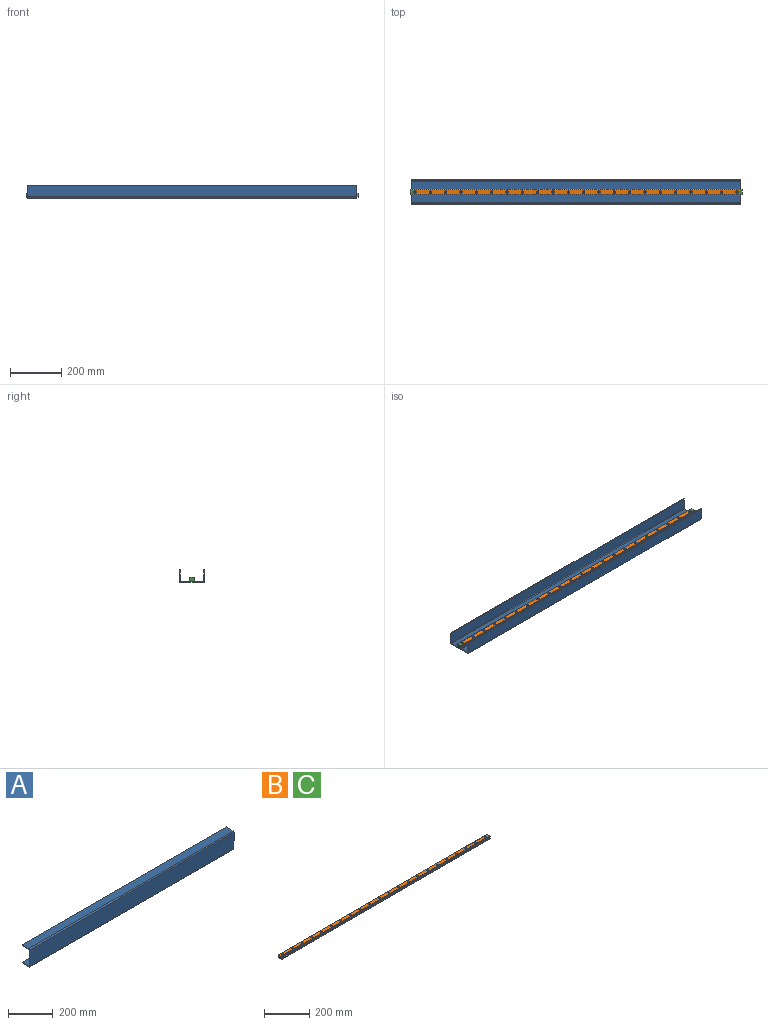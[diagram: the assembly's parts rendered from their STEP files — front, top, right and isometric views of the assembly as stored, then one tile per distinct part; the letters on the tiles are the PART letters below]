
ASSEMBLY  parts=3 mates=1
PART A: 14 faces, bbox 1290x50x100 mm
  f0: plane 1290x44mm, normal (0,0,1), area 56760mm2, adj f1,f11,f12,f13
  f1: cylinder r=6mm len=1290mm, axis (-1,0,0), area 12158mm2, adj f0,f2,f12,f13
  f2: plane 1290x88mm, normal (0,-1,0), area 113520mm2, adj f1,f3,f12,f13
  f3: cylinder r=6mm len=1290mm, axis (-1,0,0), area 12158mm2, adj f2,f4,f12,f13
  f4: plane 1290x44mm, normal (0,0,-1), area 56760mm2, adj f3,f5,f12,f13
  f5: plane 1290x4mm, normal (0,1,0), area 5160mm2, adj f4,f6,f12,f13
  f6: plane 1290x43mm, normal (0,0,1), area 55470mm2, adj f5,f7,f12,f13
  f7: cylinder r=3mm len=1290mm, axis (-1,0,0), area 6079mm2, adj f6,f8,f12,f13
  f8: plane 1290x86mm, normal (0,1,0), area 110940mm2, adj f7,f9,f12,f13
  f9: cylinder r=3mm len=1290mm, axis (-1,0,0), area 6079mm2, adj f8,f10,f12,f13
  f10: plane 1290x43mm, normal (0,0,-1), area 55470mm2, adj f9,f11,f12,f13
  f11: plane 1290x4mm, normal (0,1,0), area 5160mm2, adj f0,f10,f12,f13
  f12: plane 100x50mm, normal (1,0,0), area 756.4mm2, adj f0,f1,f2,f3,f4,f5,f6,f7
  f13: plane 100x50mm, normal (-1,0,0), area 756.4mm2, adj f0,f1,f2,f3,f4,f5,f6,f7
PART B: 100 faces, bbox 1300x20x16.5 mm
  f0: cylinder r=1.8mm len=1300mm, axis (-1,0,0), area 2943.1mm2, adj f1,f31,f32,f33
  f1: cylinder r=0.2mm len=1300mm, axis (-1,0,0), area 370.5mm2, adj f0,f2,f32,f33
  f2: plane 1300x16.31mm, normal (0,0,1), area 19645.8mm2, adj f1,f3,f32,f33,f34,f37,f40,f43
  f3: cylinder r=0.2mm len=1300mm, axis (-1,0,0), area 370.5mm2, adj f2,f4,f32,f33
  f4: cylinder r=1.8mm len=1300mm, axis (-1,0,0), area 2943mm2, adj f3,f5,f32,f33
  f5: cylinder r=0.2mm len=1300mm, axis (-1,0,0), area 364.4mm2, adj f4,f6,f32,f33
  f6: plane 1300x1.53mm, normal (0,-1,0), area 1984.4mm2, adj f5,f7,f32,f33
  f7: cylinder r=0.2mm len=1300mm, axis (-1,0,0), area 364.4mm2, adj f6,f8,f32,f33
  f8: cylinder r=1.8mm len=1300mm, axis (-1,0,0), area 3506.9mm2, adj f7,f9,f32,f33
  f9: cylinder r=0.2mm len=1300mm, axis (-1,0,0), area 228.9mm2, adj f8,f10,f32,f33
  f10: plane 1300x0.14mm, normal (0,-0.71,-0.71), area 254.9mm2, adj f9,f11,f32,f33
  f11: cylinder r=0.5mm len=1300mm, axis (-1,0,0), area 510.5mm2, adj f10,f12,f32,f33
  f12: plane 1300x4.09mm, normal (0,-1,0), area 5311.4mm2, adj f11,f13,f32,f33
  f13: cylinder r=0.5mm len=1300mm, axis (-1,0,0), area 510.5mm2, adj f12,f14,f32,f33
  f14: plane 1300x1.78mm, normal (0,-0.71,0.71), area 3273.1mm2, adj f13,f15,f32,f33
  f15: cylinder r=0.25mm len=1300mm, axis (-1,0,0), area 255.3mm2, adj f14,f16,f32,f33
  f16: plane 1300x2.9mm, normal (0,-1,0), area 3765.4mm2, adj f15,f17,f32,f33
  f17: plane 1300x1mm, normal (0,-0.71,-0.71), area 1838.4mm2, adj f16,f18,f32,f33
  f18: plane 1300x18mm, normal (0,0,-1), area 22778mm2, adj f17,f19,f32,f33,f36,f39,f42,f45
  f19: plane 1300x1mm, normal (0,0.71,-0.71), area 1838.5mm2, adj f18,f20,f32,f33
  f20: plane 1300x2.9mm, normal (0,1,0), area 3765.4mm2, adj f19,f21,f32,f33
  f21: cylinder r=0.25mm len=1300mm, axis (-1,0,0), area 255.3mm2, adj f20,f22,f32,f33
  f22: plane 1300x1.78mm, normal (0,0.71,0.71), area 3273.1mm2, adj f21,f23,f32,f33
  f23: cylinder r=0.5mm len=1300mm, axis (-1,0,0), area 510.5mm2, adj f22,f24,f32,f33
  f24: plane 1300x4.09mm, normal (0,1,0), area 5311.6mm2, adj f23,f25,f32,f33
  f25: cylinder r=0.5mm len=1300mm, axis (-1,0,0), area 510.5mm2, adj f24,f26,f32,f33
  f26: plane 1300x0.14mm, normal (0,0.71,-0.71), area 254.8mm2, adj f25,f27,f32,f33
  f27: cylinder r=0.2mm len=1300mm, axis (-1,0,0), area 228.9mm2, adj f26,f28,f32,f33
  f28: cylinder r=1.8mm len=1300mm, axis (-1,0,0), area 3506.9mm2, adj f27,f29,f32,f33
  f29: cylinder r=0.2mm len=1300mm, axis (-1,0,0), area 364.4mm2, adj f28,f30,f32,f33
  f30: plane 1300x1.53mm, normal (0,1,0), area 1984.4mm2, adj f29,f31,f32,f33
  f31: cylinder r=0.2mm len=1300mm, axis (-1,0,0), area 364.4mm2, adj f0,f30,f32,f33
  f32: plane 20x16.5mm, normal (1,0,0), area 295.9mm2, adj f0,f1,f2,f3,f4,f5,f6,f7
  f33: plane 20x16.5mm, normal (-1,0,0), area 295.9mm2, adj f0,f1,f2,f3,f4,f5,f6,f7
  f34: cylinder r=4.75mm len=9.5mm, axis (0,0,1), area 253.7mm2, adj f2,f35
  f35: plane 9.5x9.5mm, normal (0,0,1), area 42.6mm2, adj f34,f36
  f36: cylinder r=3mm len=8mm, axis (0,0,1), area 150.8mm2, adj f18,f35
  f37: cylinder r=4.75mm len=9.5mm, axis (0,0,1), area 253.7mm2, adj f2,f38
  f38: plane 9.5x9.5mm, normal (0,0,1), area 42.6mm2, adj f37,f39
  f39: cylinder r=3mm len=8mm, axis (0,0,1), area 150.8mm2, adj f18,f38
  f40: cylinder r=4.75mm len=9.5mm, axis (0,0,1), area 253.7mm2, adj f2,f41
  f41: plane 9.5x9.5mm, normal (0,0,1), area 42.6mm2, adj f40,f42
  f42: cylinder r=3mm len=8mm, axis (0,0,1), area 150.8mm2, adj f18,f41
  f43: cylinder r=4.75mm len=9.5mm, axis (0,0,1), area 253.7mm2, adj f2,f44
  f44: plane 9.5x9.5mm, normal (0,0,1), area 42.6mm2, adj f43,f45
  f45: cylinder r=3mm len=8mm, axis (0,0,1), area 150.8mm2, adj f18,f44
  f46: cylinder r=4.75mm len=9.5mm, axis (0,0,1), area 253.7mm2, adj f2,f47
  f47: plane 9.5x9.5mm, normal (0,0,1), area 42.6mm2, adj f46,f48
  f48: cylinder r=3mm len=8mm, axis (0,0,1), area 150.8mm2, adj f18,f47
  f49: cylinder r=4.75mm len=9.5mm, axis (0,0,1), area 253.7mm2, adj f2,f50
  f50: plane 9.5x9.5mm, normal (0,0,1), area 42.6mm2, adj f49,f51
  f51: cylinder r=3mm len=8mm, axis (0,0,1), area 150.8mm2, adj f18,f50
  f52: cylinder r=4.75mm len=9.5mm, axis (0,0,1), area 253.7mm2, adj f2,f53
  f53: plane 9.5x9.5mm, normal (0,0,1), area 42.6mm2, adj f52,f54
  f54: cylinder r=3mm len=8mm, axis (0,0,1), area 150.8mm2, adj f18,f53
  f55: cylinder r=4.75mm len=9.5mm, axis (0,0,1), area 253.7mm2, adj f2,f56
  f56: plane 9.5x9.5mm, normal (0,0,1), area 42.6mm2, adj f55,f57
  f57: cylinder r=3mm len=8mm, axis (0,0,1), area 150.8mm2, adj f18,f56
  f58: cylinder r=4.75mm len=9.5mm, axis (0,0,1), area 253.7mm2, adj f2,f59
  f59: plane 9.5x9.5mm, normal (0,0,1), area 42.6mm2, adj f58,f60
  f60: cylinder r=3mm len=8mm, axis (0,0,1), area 150.8mm2, adj f18,f59
  f61: cylinder r=4.75mm len=9.5mm, axis (0,0,1), area 253.7mm2, adj f2,f62
  f62: plane 9.5x9.5mm, normal (0,0,1), area 42.6mm2, adj f61,f63
  f63: cylinder r=3mm len=8mm, axis (0,0,1), area 150.8mm2, adj f18,f62
  f64: cylinder r=4.75mm len=9.5mm, axis (0,0,1), area 253.7mm2, adj f2,f65
  f65: plane 9.5x9.5mm, normal (0,0,1), area 42.6mm2, adj f64,f66
  f66: cylinder r=3mm len=8mm, axis (0,0,1), area 150.8mm2, adj f18,f65
  f67: cylinder r=4.75mm len=9.5mm, axis (0,0,1), area 253.7mm2, adj f2,f68
  f68: plane 9.5x9.5mm, normal (0,0,1), area 42.6mm2, adj f67,f69
  f69: cylinder r=3mm len=8mm, axis (0,0,1), area 150.8mm2, adj f18,f68
  f70: cylinder r=4.75mm len=9.5mm, axis (0,0,1), area 253.7mm2, adj f2,f71
  f71: plane 9.5x9.5mm, normal (0,0,1), area 42.6mm2, adj f70,f72
  f72: cylinder r=3mm len=8mm, axis (0,0,1), area 150.8mm2, adj f18,f71
  f73: cylinder r=4.75mm len=9.5mm, axis (0,0,1), area 253.7mm2, adj f2,f74
  f74: plane 9.5x9.5mm, normal (0,0,1), area 42.6mm2, adj f73,f75
  f75: cylinder r=3mm len=8mm, axis (0,0,1), area 150.8mm2, adj f18,f74
  f76: cylinder r=4.75mm len=9.5mm, axis (0,0,1), area 253.7mm2, adj f2,f77
  f77: plane 9.5x9.5mm, normal (0,0,1), area 42.6mm2, adj f76,f78
  f78: cylinder r=3mm len=8mm, axis (0,0,1), area 150.8mm2, adj f18,f77
  f79: cylinder r=4.75mm len=9.5mm, axis (0,0,1), area 253.7mm2, adj f2,f80
  f80: plane 9.5x9.5mm, normal (0,0,1), area 42.6mm2, adj f79,f81
  f81: cylinder r=3mm len=8mm, axis (0,0,1), area 150.8mm2, adj f18,f80
  f82: cylinder r=4.75mm len=9.5mm, axis (0,0,1), area 253.7mm2, adj f2,f83
  f83: plane 9.5x9.5mm, normal (0,0,1), area 42.6mm2, adj f82,f84
  f84: cylinder r=3mm len=8mm, axis (0,0,1), area 150.8mm2, adj f18,f83
  f85: cylinder r=4.75mm len=9.5mm, axis (0,0,1), area 253.7mm2, adj f2,f86
  f86: plane 9.5x9.5mm, normal (0,0,1), area 42.6mm2, adj f85,f87
  f87: cylinder r=3mm len=8mm, axis (0,0,1), area 150.8mm2, adj f18,f86
  f88: cylinder r=4.75mm len=9.5mm, axis (0,0,1), area 253.7mm2, adj f2,f89
  f89: plane 9.5x9.5mm, normal (0,0,1), area 42.6mm2, adj f88,f90
  f90: cylinder r=3mm len=8mm, axis (0,0,1), area 150.8mm2, adj f18,f89
  f91: cylinder r=4.75mm len=9.5mm, axis (0,0,1), area 253.7mm2, adj f2,f92
  f92: plane 9.5x9.5mm, normal (0,0,1), area 42.6mm2, adj f91,f93
  f93: cylinder r=3mm len=8mm, axis (0,0,1), area 150.8mm2, adj f18,f92
  f94: cylinder r=4.75mm len=9.5mm, axis (0,0,1), area 253.7mm2, adj f2,f95
  f95: plane 9.5x9.5mm, normal (0,0,1), area 42.6mm2, adj f94,f96
  f96: cylinder r=3mm len=8mm, axis (0,0,1), area 150.8mm2, adj f18,f95
  f97: cylinder r=4.75mm len=9.5mm, axis (0,0,1), area 253.7mm2, adj f2,f98
  f98: plane 9.5x9.5mm, normal (0,0,1), area 42.6mm2, adj f97,f99
  f99: cylinder r=3mm len=8mm, axis (0,0,1), area 150.8mm2, adj f18,f98
PART C: same geometry as B
PLACE A rot(axis=(1,0,0),90deg) t=(-195.12,156.64,-241.92)mm
PLACE B t=(-200.12,106.12,-228.04)mm
PLACE C t=(-200.12,106.12,-228.04)mm
MATE fastened A.f8 <-> B.f18  axis (0,0,1) through (449.88,106.64,-237.92)mm
